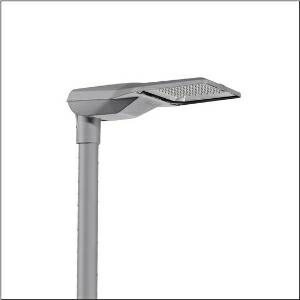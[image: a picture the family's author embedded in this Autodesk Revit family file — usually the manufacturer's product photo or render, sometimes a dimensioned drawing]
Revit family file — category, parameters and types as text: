
# Revit family: streetlight_sl_21_iq_midi___stw1_0a_5xe3e21d08nb_941d
name_source: partatom
category: Lighting Fixtures
units: mm (PartAtom-declared; Revit-internal decimal feet)

## family parameters
Cut with Voids When Loaded = No
Host = Face
Light Source = No
Part Type = Normal
Room Calculation Point = No
Round Connector Dimension = Use Diameter
Shared = No

## types (1)
- --- (1 x LED, 19210 lm, 155.5 W, 2200K)
    Apparent Load = 155 VA
    CIE Flux Codes = 39 75 98 100 100
    Color Rendering = 70
    Color Temperature = 2200K
    Default Elevation = 1800 mm
    Description = Streetlight SL 21 iQ midi, mast luminaire, primary light control with lens, of PMMA, primary optical cover: cover, of toughened safety glass, transparent, light distribution: STW1.0a, light emission: direct distribution, primary light characteristic: asymmetric, installation type: post-top, side-entry, LED, High Power LED, rated luminous flux: 19.210lm, luminous efficacy: 124lm/W, light colour: 722, colour temperature: 2200K, control gear: iQ-Comfort, control: Auto-Match, Temp-Guard, Lumen-Switch, Night-Set, Smart-Wire, Light-Fading, Desk-Remote (wireless, voltage-free reading and setting of iQ features in the workshop via application-optimized NFC function/RFID function), optimised constant luminous flux control (CLO 2.0), pre-setting: linear dimming characteristic, mains connection: 230..240V, AC, 50/60Hz, start of lifetime: 156W, end of service life: 162W, reduction: 69W, luminaire housing, of diecast aluminium, powder-coated, Siteco® metallic grey (DB 702S), corrosivity category C5 mid according to DIN EN ISO 12944, please order mast flange separately, inclination adjustable: 0°, 5°, 10°, 15°, sealing non-destructively replaceable, multi-level sealing system, length: 644mm, width: 335mm, height: 110mm, mast flange for spigot size: 42mm (side-entry): 5XC10008XM4, 60/48mm (side-entry/post-top): 5XC10108XM2, 76/60mm (side-entry/post-top): 5XC10108XM1, mounting height: 4..8m, protection rating (complete): IP66, insulation class (complete): insulation class II (safety insulation), certification: CE, ENEC, ENEC+, VDE, impact resistance: IK10, permissible operating ambient temperature for outdoor applications: -40..+50°C, standard-compliant lighting for roads and squares, packaging unit: 1 piece

Light Distribution: STW1.0a
    Height = 111 mm
    Lamp = 1 x LED
    Lamp Light Flux = 19210 lm
    Lamp Power = 155.5 W
    Lamp count = 1
    Length = 644 mm
    Luminous efficacy = 124 lm/W
    Manufacturer = Siteco
    ModVariant = No
    Model = 5XE3E21D08NB
    Number of Poles = 1
    OnlyDefault = Yes
    Power Factor = 1
    Product Name = Streetlight SL 21 iQ midi | STW1.0a
    Product group = mast luminaire | pylon top
    ProductGroupID = 6100
    Protection Class = Protection class II
    Protection Degree = IP 66
    RLX_Detail_Level = 1
    RLX_Emergency_Light_Flux = 0 lm
    RLX_Emergency_Type = 0
    RLX_Emergency_Type_DB = No
    RlxData = <blob elided: 27305 chars, md5=f924cf74>
    Socket = socket
    Standby Power = 0 W
    System Light Flux = 19210 lm
    System Power = 155 W
    Type Comments = factory setting: luminous flux: 100 % | dim-lin: 254 | 823 mA
    Type Image = l_1004298.jpg
    URL = http://relux.com
    VarID = @adj_191469
    Voltage = 0 V
    Weight = 0.00 kg
    Width = 336 mm

## geometry (parser evidence)
native form markers: Blend x4, Sweep x13
no freeform markers — native parametric forms only
